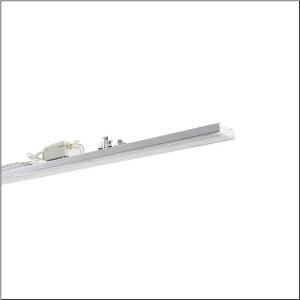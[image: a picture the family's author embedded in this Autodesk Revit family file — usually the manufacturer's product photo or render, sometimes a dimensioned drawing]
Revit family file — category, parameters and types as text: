
# Revit family: licross_r__21_recessed_mo_52tl14de445g_3a0e
name_source: partatom
category: Lighting Fixtures
units: mm (PartAtom-declared; Revit-internal decimal feet)

## family parameters
Cut with Voids When Loaded = No
Host = Face
Light Source = No
Part Type = Normal
Room Calculation Point = No
Round Connector Dimension = Use Diameter
Shared = No

## types (1)
- --- (1 x LED, 4730 lm, 29.9 W, 4000K)
    Apparent Load = 30 VA
    CIE Flux Codes = 56 84 97 100 100
    Color Rendering = 80
    Color Temperature = 4000K
    Default Elevation = 1800 mm
    Description = Licross® 21 Recessed MO, luminaire insert, of sheet steel, galvanised, coil coated, white, length: 750mm, width: 66mm, height: 67mm, LED rated luminous flux: 4.730lm, light colour: 840, control gear: DALI 2, with plug, 5-pole, with phase selection, mains connection: 220..240V, AC, 50/60Hz, rated input power: 30W, halogen-free wiring, primary light control with lens, of plastic, primary optical cover: cover, of PMMA, light emission: direct distribution, primary light characteristic: asymmetric, protection rating (complete): IP40, insulation class (complete): insulation class I (protective earthing), certification: CE, ENEC, VDE, UKCA, protection symbol: D if used in an environment without relevant dust loads with corresponding accessories, impact resistance: IK06, permissible ambient temperature for indoor applications: -25..+35°C, corresponds to IFS (International Featured Standards) requirements for safety and quality in the food industry, reducing of maximum allowable ambient temperature of 5°C with ceiling mounting, LABS conformity tested according to VDMA 24364:2018-05, packaging unit: 1 piece
    Height = 58 mm
    Lamp = 1 x LED
    Lamp Light Flux = 4730 lm
    Lamp Power = 29.9 W
    Lamp count = 1
    Length = 750 mm
    Luminous efficacy = 158 lm/W
    Manufacturer = Siteco
    ModVariant = No
    Model = 52TL14DE445G
    Mounting Place = Ceiling
    Mounting Type = Pendant
    Number of Poles = 1
    OnlyDefault = Yes
    Power Factor = 1
    Product Name = Licross® 21 Recessed MO
    Product group = luminaire insert
    ProductGroupID = 901
    Protection Class = Protection class I
    Protection Degree = IP 40
    RLX_Detail_Level = 1
    RLX_Emergency_Light_Flux = 0 lm
    RLX_Emergency_Type = 0
    RLX_Emergency_Type_DB = No
    RlxData = <blob elided: 29285 chars, md5=54fbe981>
    Socket = socket
    Standby Power = 0 W
    System Light Flux = 4730 lm
    System Power = 30 W
    Type Comments = factory setting: luminous flux: 100 % | dim-lin: 254 | 390 mA
    Type Image = l_1296930.jpg
    URL = http://relux.com
    VarID = @adj_059495
    Voltage = 0 V
    Weight = 0.00 kg
    Width = 66 mm

## geometry (parser evidence)
native form markers: Blend x4, Sweep x11
no freeform markers — native parametric forms only
